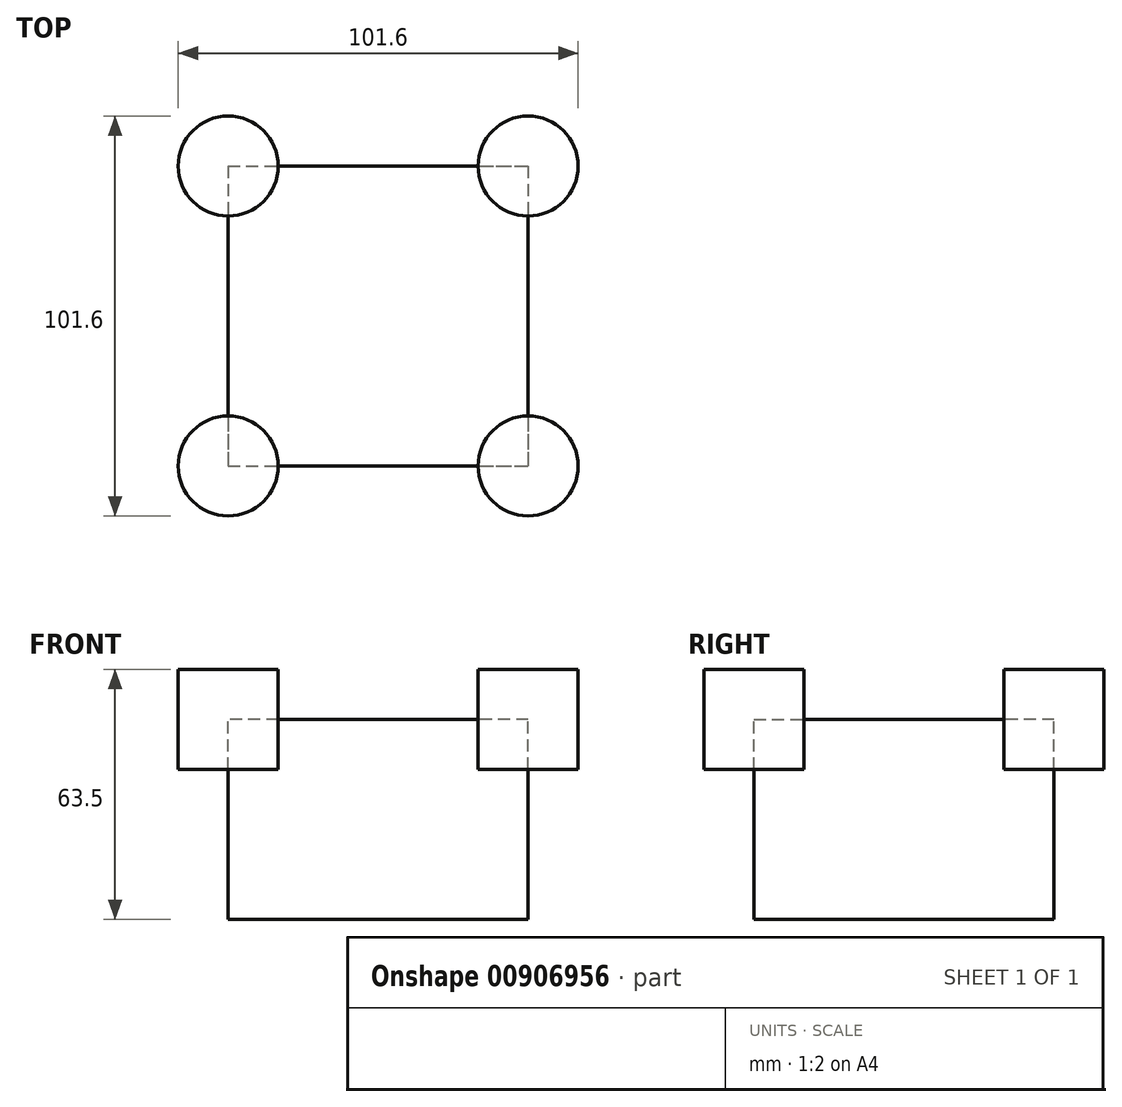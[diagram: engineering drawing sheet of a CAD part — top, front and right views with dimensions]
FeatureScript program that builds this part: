
annotation { "Feature Type Name" : "Feature", "Feature Type Description" : "" }
export const myFeature = defineFeature(function(context is Context, id is Id, definition is map)
    precondition{}
    {
        {
            var Q0;
            Q0=qCreatedBy(makeId("Top.planeOp"),FACE);
            var sketch = newSketch(context, id + "F0", { "sketchPlane" : qUnion([Q0])});
            skLineSegment(sketch, "E0.bottom", {"start": v(-38.1, 38.1) * mm, "end": v(38.1, 38.1) * mm});
            skLineSegment(sketch, "E0.top", {"start": v(-38.1, -38.1) * mm, "end": v(38.1, -38.1) * mm});
            skLineSegment(sketch, "E0.left", {"start": v(-38.1, 38.1) * mm, "end": v(-38.1, -38.1) * mm});
            skLineSegment(sketch, "E0.right", {"start": v(38.1, 38.1) * mm, "end": v(38.1, -38.1) * mm});
            skLineSegment(sketch, "E1", {"start": v(-38.1, 0) * mm, "end": v(38.1, 0) * mm, "construction": true});
            skSolve(sketch);
        }
        {
            var Q0;
            Q0=makeQuery(id+"F0.imprint","IMPRINT",FACE,{"disambiguationData":[TD([[makeQuery(id+"F0.imprint","IMPRINT",EDGE,{"derivedFrom":sQuery(id+"F0.wireOp",EDGE,"E0.bottom")}),-1.0]])]});
            extrude(context, id + "F1", {"entities" : qUnion([Q0]), "depth" : 50.8 * mm, "offsetDistance" : 25.4 * mm});
        }
        {
            var Q0;
            Q0=makeQuery(id+"F1.opExtrude","CAP_FACE",FACE,{"disambiguationData":[OSD([sQuery(id+"F0.wireOp",EDGE,"E0.bottom"),sQuery(id+"F0.wireOp",EDGE,"E0.top"),sQuery(id+"F0.wireOp",EDGE,"E0.left"),sQuery(id+"F0.wireOp",EDGE,"E0.right")])],"isStart":false});
            var sketch = newSketch(context, id + "F2", { "sketchPlane" : qUnion([Q0])});
            skCircle(sketch, "E2", {"center": v(-38.1, 38.1) * mm, "radius": 12.7 * mm});
            skLineSegment(sketch, "E3", {"start": v(0, 38.1) * mm, "end": v(0, -38.1) * mm, "construction": true});
            skCircle(sketch, "E4.MirrorC", {"center": v(38.1, 38.1) * mm, "radius": 12.7 * mm});
            skCircle(sketch, "E5.MirrorC", {"center": v(38.1, -38.1) * mm, "radius": 12.7 * mm});
            skCircle(sketch, "E6.MirrorC", {"center": v(-38.1, -38.1) * mm, "radius": 12.7 * mm});
            skSolve(sketch);
        }
        {
            var Q0;
            Q0 = qSketchRegion(id + "F2", true);
            extrude(context, id + "F3", {"entities" : qUnion([Q0]), "operationType" : NewBodyOperationType.ADD, "endBound" : BoundingType.SYMMETRIC, "oppositeDirection" : true, "depth" : 25.4 * mm, "offsetDistance" : 25.4 * mm});
        }
    });
